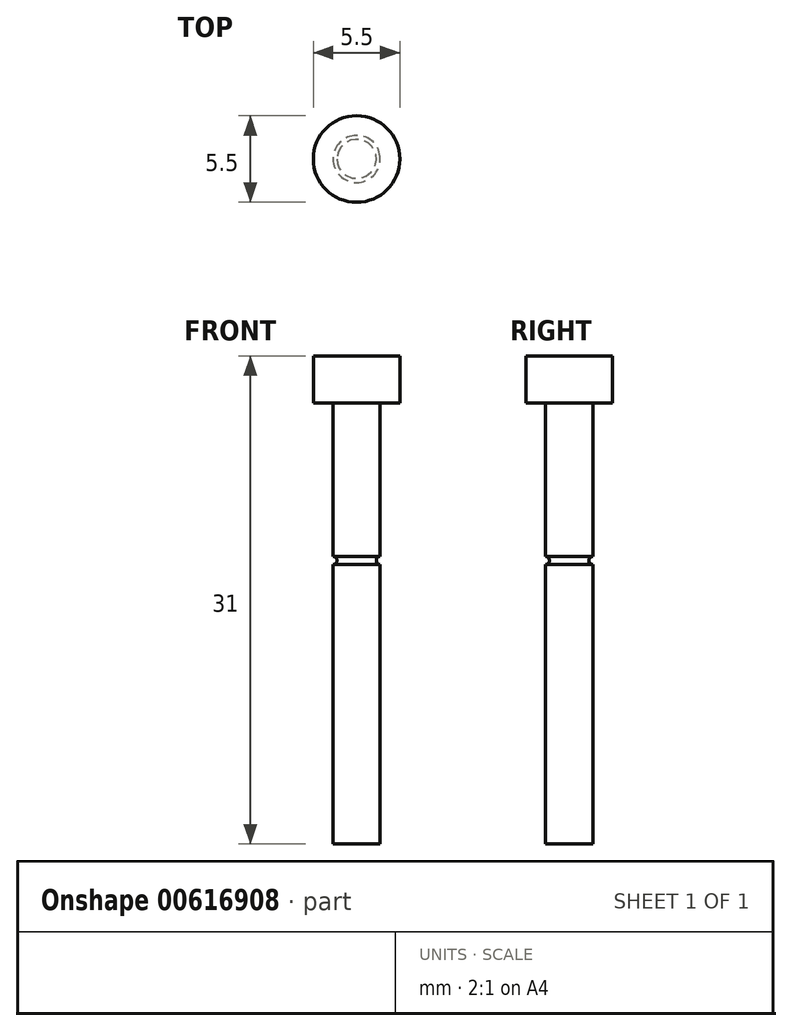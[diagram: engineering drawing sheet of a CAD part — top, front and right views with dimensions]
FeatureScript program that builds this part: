
annotation { "Feature Type Name" : "Feature", "Feature Type Description" : "" }
export const myFeature = defineFeature(function(context is Context, id is Id, definition is map)
    precondition{}
    {
        {
            var Q0;
            Q0=qCreatedBy(makeId("Front.planeOp"),FACE);
            var sketch = newSketch(context, id + "F0", { "sketchPlane" : qUnion([Q0])});
            skLineSegment(sketch, "E0", {"start": v(0, 0) * mm, "end": v(0, 31) * mm});
            skLineSegment(sketch, "E1", {"start": v(0, 0) * mm, "end": v(1.5, 0) * mm});
            skLineSegment(sketch, "E2", {"start": v(1.5, 0) * mm, "end": v(1.5, 17.75) * mm});
            skLineSegment(sketch, "E3", {"start": v(1.5, 28) * mm, "end": v(2.75, 28) * mm});
            skLineSegment(sketch, "E4", {"start": v(2.75, 28) * mm, "end": v(2.75, 31) * mm});
            skLineSegment(sketch, "E5", {"start": v(2.75, 31) * mm, "end": v(0, 31) * mm});
            skArc(sketch, "E6", {"start": v(1.5, 18.25) * mm, "mid": v(1.25, 18) * mm, "end": v(1.5, 17.75) * mm});
            skLineSegment(sketch, "E7.trimOffspring", {"start": v(1.5, 18.25) * mm, "end": v(1.5, 28) * mm});
            skSolve(sketch);
        }
        {
            var Q0;
            Q0 = qSketchRegion(id + "F0", true);
            var Q1;
            Q1=sQuery(id+"F0.wireOp",EDGE,"E0");
            revolve(context, id + "F1", {"entities" : qUnion([Q0]), "axis" : qUnion([Q1]), "revolveType" : RevolveType.FULL});
        }
    });
